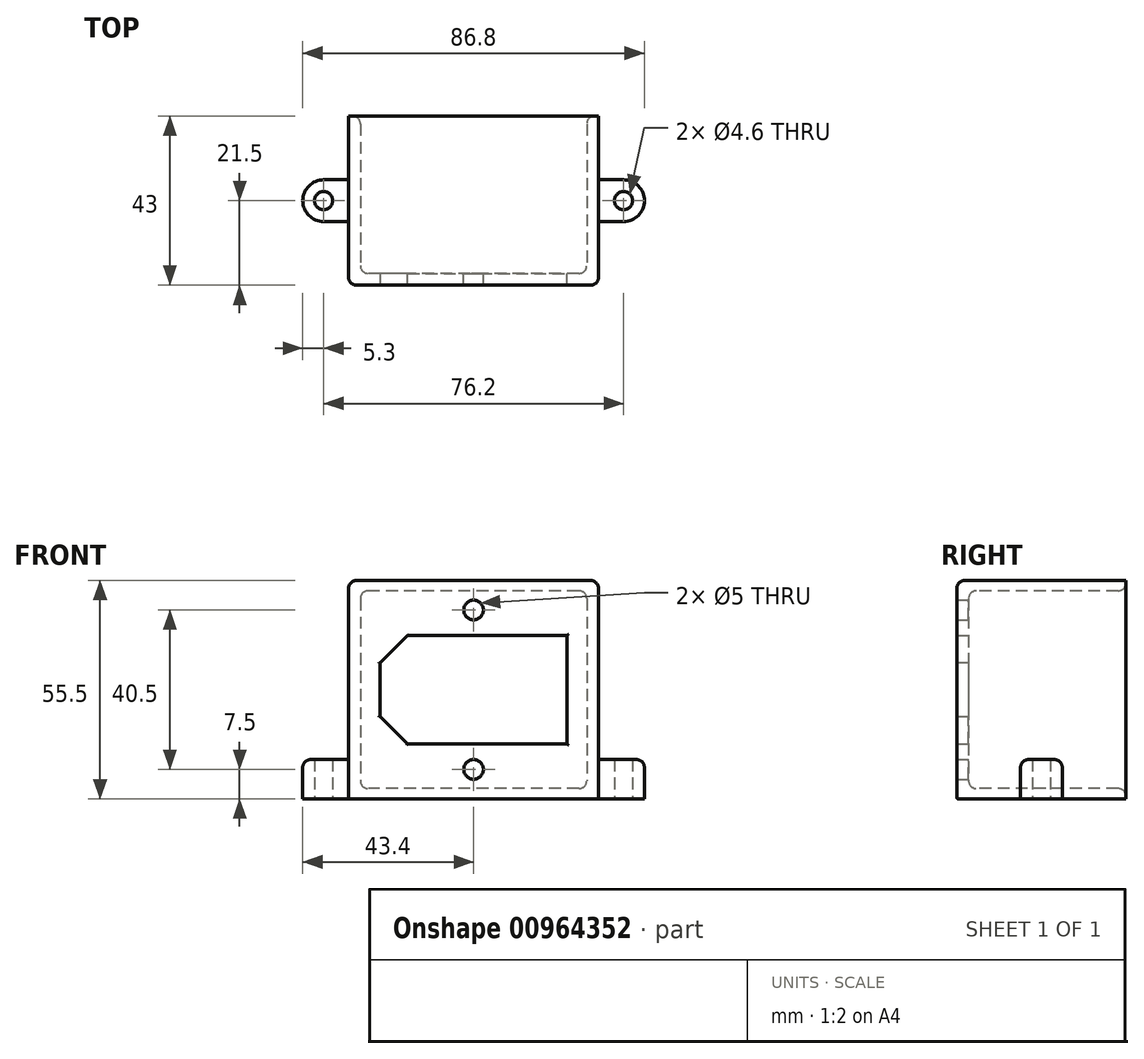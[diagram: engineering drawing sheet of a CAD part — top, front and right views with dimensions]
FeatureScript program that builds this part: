
annotation { "Feature Type Name" : "Feature", "Feature Type Description" : "" }
export const myFeature = defineFeature(function(context is Context, id is Id, definition is map)
    precondition{}
    {
        {
            var Q0;
            Q0=qCreatedBy(makeId("Front.planeOp"),FACE);
            var sketch = newSketch(context, id + "F0", { "sketchPlane" : qUnion([Q0])});
            skLineSegment(sketch, "E0.bottom", {"start": v(0, 0) * mm, "end": v(-63.5, 0) * mm});
            skLineSegment(sketch, "E0.top", {"start": v(0, 55.5) * mm, "end": v(-63.5, 55.5) * mm});
            skLineSegment(sketch, "E0.left", {"start": v(0, 0) * mm, "end": v(0, 55.5) * mm});
            skLineSegment(sketch, "E0.right", {"start": v(-63.5, 0) * mm, "end": v(-63.5, 55.5) * mm});
            skLineSegment(sketch, "E1.bottom", {"start": v(-55.5, 41.5) * mm, "end": v(-8, 41.5) * mm});
            skLineSegment(sketch, "E1.top", {"start": v(-55.5, 14) * mm, "end": v(-8, 14) * mm});
            skLineSegment(sketch, "E1.left", {"start": v(-55.5, 41.5) * mm, "end": v(-55.5, 14) * mm});
            skLineSegment(sketch, "E1.right", {"start": v(-8, 41.5) * mm, "end": v(-8, 14) * mm});
            skLineSegment(sketch, "E2", {"start": v(-31.75, 55.5) * mm, "end": v(-31.75, 0) * mm, "construction": true});
            skPoint(sketch, "E3", {"position": v(-31.75, 41.5) * mm});
            skLineSegment(sketch, "E4", {"start": v(-34.25, 55.5) * mm, "end": v(-34.25, 0) * mm, "construction": true});
            skCircle(sketch, "E5", {"center": v(-31.75, 48) * mm, "radius": 2.5 * mm});
            skCircle(sketch, "E6", {"center": v(-31.75, 7.5) * mm, "radius": 2.5 * mm});
            skLineSegment(sketch, "E7", {"start": v(-55.5, 27.75) * mm, "end": v(-8, 27.75) * mm, "construction": true});
            skLineSegment(sketch, "E8.bottom", {"start": v(-8, 48) * mm, "end": v(-55.5, 48) * mm, "construction": true});
            skLineSegment(sketch, "E8.top", {"start": v(-8, 7.5) * mm, "end": v(-55.5, 7.5) * mm, "construction": true});
            skLineSegment(sketch, "E8.left", {"start": v(-8, 48) * mm, "end": v(-8, 7.5) * mm, "construction": true});
            skLineSegment(sketch, "E8.right", {"start": v(-55.5, 48) * mm, "end": v(-55.5, 7.5) * mm, "construction": true});
            skPoint(sketch, "E8.middle", {"position": v(-31.75, 27.75) * mm});
            skLineSegment(sketch, "E9", {"start": v(0, 55.5) * mm, "end": v(-63.5, 0) * mm, "construction": true});
            skLineSegment(sketch, "E10.bottom", {"start": v(-3, 52.88) * mm, "end": v(-60.5, 52.88) * mm});
            skLineSegment(sketch, "E10.top", {"start": v(-3, 2.62) * mm, "end": v(-60.5, 2.62) * mm});
            skLineSegment(sketch, "E10.left", {"start": v(-3, 52.88) * mm, "end": v(-3, 2.62) * mm});
            skLineSegment(sketch, "E10.right", {"start": v(-60.5, 52.88) * mm, "end": v(-60.5, 2.62) * mm});
            skSolve(sketch);
        }
        {
            var Q0;
            Q0 = qSketchRegion(id + "F0", true);
            var Q1;
            Q1=makeQuery(id+"F0.imprint","IMPRINT",FACE,{"disambiguationData":[TD([[makeQuery(id+"F0.imprint","IMPRINT",EDGE,{"derivedFrom":sQuery(id+"F0.wireOp",EDGE,"E1.bottom")}),1.0]])]});
            extrude(context, id + "F1", {"entities" : qUnion([Q0, Q1]), "depth" : 3 * mm, "offsetDistance" : 25 * mm});
        }
        {
            var Q0;
            Q0=makeQuery(id+"F1.opExtrude","SWEPT_EDGE",EDGE,{"disambiguationData":[OSD([sQuery(id+"F0.wireOp",EDGE,"E1.bottom"),sQuery(id+"F0.wireOp",EDGE,"E1.left")])]});
            var Q1;
            Q1=makeQuery(id+"F1.opExtrude","SWEPT_EDGE",EDGE,{"disambiguationData":[OSD([sQuery(id+"F0.wireOp",EDGE,"E1.top"),sQuery(id+"F0.wireOp",EDGE,"E1.left")])]});
            chamfer(context, id + "F2", {"entities" : qUnion([Q0, Q1]), "width" : 7 * mm, "tangentPropagation" : true});
        }
        {
            var Q0;
            Q0=makeQuery(id+"F0.imprint","IMPRINT",FACE,{"disambiguationData":[TD([[makeQuery(id+"F0.imprint","IMPRINT",EDGE,{"derivedFrom":sQuery(id+"F0.wireOp",EDGE,"E0.bottom")}),-1.0]])]});
            extrude(context, id + "F3", {"entities" : qUnion([Q0]), "operationType" : NewBodyOperationType.ADD, "oppositeDirection" : true, "depth" : 40 * mm, "offsetDistance" : 25 * mm});
        }
        {
            var Q0;
            {var subQ0=sQuery(id+"F0.wireOp",EDGE,"E0.bottom");Q0=makeQuery(id+"F3.boolean.opBoolean","MERGE",FACE,{"derivedFrom":[makeQuery(id+"F1.opExtrude","SWEPT_FACE",FACE,{"disambiguationData":[OSD([subQ0])]}),makeQuery(id+"F3.opExtrude","SWEPT_FACE",FACE,{"disambiguationData":[OSD([subQ0])]})]});}
            var sketch = newSketch(context, id + "F4", { "sketchPlane" : qUnion([Q0])});
            skLineSegment(sketch, "E11.0.0", {"start": v(-63.5, 3) * mm, "end": v(-63.5, -40) * mm, "construction": true});
            skLineSegment(sketch, "E11.0.1", {"start": v(-63.5, -40) * mm, "end": v(0, -40) * mm, "construction": true});
            skLineSegment(sketch, "E11.0.2", {"start": v(0, -40) * mm, "end": v(0, 3) * mm, "construction": true});
            skLineSegment(sketch, "E11.0.3", {"start": v(0, 3) * mm, "end": v(-63.5, 3) * mm, "construction": true});
            skLineSegment(sketch, "E12", {"start": v(-63.5, -18.5) * mm, "end": v(0, -18.5) * mm, "construction": true});
            skLineSegment(sketch, "E13", {"start": v(0, 3) * mm, "end": v(-63.5, -40) * mm, "construction": true});
            skLineSegment(sketch, "E14.bottom", {"start": v(6.35, 7.3) * mm, "end": v(-69.85, 7.3) * mm, "construction": true});
            skLineSegment(sketch, "E14.top", {"start": v(6.35, -44.3) * mm, "end": v(-69.85, -44.3) * mm, "construction": true});
            skLineSegment(sketch, "E14.left", {"start": v(6.35, 7.3) * mm, "end": v(6.35, -44.3) * mm, "construction": true});
            skLineSegment(sketch, "E14.right", {"start": v(-69.85, 7.3) * mm, "end": v(-69.85, -44.3) * mm, "construction": true});
            skPoint(sketch, "E14.middle", {"position": v(-31.75, -18.5) * mm});
            skCircle(sketch, "E15", {"center": v(-69.85, -18.5) * mm, "radius": 2.3 * mm});
            skLineSegment(sketch, "E16", {"start": v(-63.5, -13.2) * mm, "end": v(0, -13.2) * mm, "construction": true});
            skCircle(sketch, "E17", {"center": v(-69.85, -18.5) * mm, "radius": 5.3 * mm});
            skLineSegment(sketch, "E18", {"start": v(-63.5, -16.2) * mm, "end": v(0, -16.2) * mm, "construction": true});
            skCircle(sketch, "E19", {"center": v(6.35, -18.5) * mm, "radius": 2.3 * mm});
            skCircle(sketch, "E20", {"center": v(6.35, -18.5) * mm, "radius": 5.3 * mm});
            skLineSegment(sketch, "E21", {"start": v(-69.85, -13.2) * mm, "end": v(-63.5, -13.2) * mm});
            skLineSegment(sketch, "E22", {"start": v(-69.85, -23.8) * mm, "end": v(-63.5, -23.8) * mm});
            skLineSegment(sketch, "E23", {"start": v(6.35, -13.2) * mm, "end": v(0, -13.2) * mm});
            skLineSegment(sketch, "E24", {"start": v(6.35, -23.8) * mm, "end": v(0, -23.8) * mm});
            skSolve(sketch);
        }
        {
            var Q0;
            Q0 = qSketchRegion(id + "F4", true);
            var Q1;
            {var subQ0=sQuery(id+"F4.wireOp",EDGE,"E21");Q1=makeQuery(id+"F4.imprint","IMPRINT",FACE,{"disambiguationData":[TD([[makeQuery(id+"F4.imprint","IMPRINT",EDGE,{"derivedFrom":subQ0}),-1.0]])]});}
            var Q2;
            {var subQ0=sQuery(id+"F4.wireOp",EDGE,"E23");Q2=makeQuery(id+"F4.imprint","IMPRINT",FACE,{"disambiguationData":[TD([[makeQuery(id+"F4.imprint","IMPRINT",EDGE,{"derivedFrom":subQ0}),1.0]])]});}
            var Q3;
            {var subQ0=sQuery(id+"F0.wireOp",EDGE,"E0.top");Q3=makeQuery(id+"F3.boolean.opBoolean","MERGE",FACE,{"derivedFrom":[makeQuery(id+"F1.opExtrude","SWEPT_FACE",FACE,{"disambiguationData":[OSD([subQ0])]}),makeQuery(id+"F3.opExtrude","SWEPT_FACE",FACE,{"disambiguationData":[OSD([subQ0])]})]});}
            extrude(context, id + "F5", {"entities" : qUnion([Q0, Q1, Q2]), "operationType" : NewBodyOperationType.ADD, "oppositeDirection" : true, "depth" : 10 * mm, "endBoundEntityFace" : qUnion([Q3]), "offsetDistance" : 25 * mm});
        }
        {
            var Q0;
            {var subQ0=sQuery(id+"F0.wireOp",EDGE,"E10.left");var subQ1=sQuery(id+"F0.wireOp",EDGE,"E10.top");var subQ2=sQuery(id+"F0.wireOp",EDGE,"E10.bottom");Q0=makeQuery(id+"F5.boolean.opBoolean","SPLIT",FACE,{"disambiguationData":[TD([makeQuery(id+"F3.opExtrude","CAP_FACE",FACE,{"disambiguationData":[OSD([sQuery(id+"F0.wireOp",EDGE,"E0.bottom"),sQuery(id+"F0.wireOp",EDGE,"E0.top"),sQuery(id+"F0.wireOp",EDGE,"E0.left"),sQuery(id+"F0.wireOp",EDGE,"E0.right"),subQ2,subQ1,subQ0,sQuery(id+"F0.wireOp",EDGE,"E10.right")])],"isStart":false})])],"derivedFrom":makeQuery(id+"F3.opExtrude","SWEPT_FACE",FACE,{"disambiguationData":[OSD([subQ0])]})});}
            var Q1;
            Q1=makeQuery(id+"F5.boolean.opBoolean","SPLIT",FACE,{"disambiguationData":[TD([makeQuery(id+"F1.opExtrude","CAP_FACE",FACE,{"disambiguationData":[OSD([sQuery(id+"F0.wireOp",EDGE,"E0.bottom"),sQuery(id+"F0.wireOp",EDGE,"E0.top"),sQuery(id+"F0.wireOp",EDGE,"E0.left"),sQuery(id+"F0.wireOp",EDGE,"E0.right"),sQuery(id+"F0.wireOp",EDGE,"E1.bottom"),sQuery(id+"F0.wireOp",EDGE,"E1.top"),sQuery(id+"F0.wireOp",EDGE,"E1.left"),sQuery(id+"F0.wireOp",EDGE,"E1.right"),sQuery(id+"F0.wireOp",EDGE,"E5"),sQuery(id+"F0.wireOp",EDGE,"E6")])],"isStart":true})])],"derivedFrom":makeQuery(id+"F3.opExtrude","SWEPT_FACE",FACE,{"disambiguationData":[OSD([sQuery(id+"F0.wireOp",EDGE,"E10.left")])]})});
            var Q2;
            {var subQ2=sQuery(id+"F0.wireOp",EDGE,"E10.top");Q2=makeQuery(id+"F5.boolean.opBoolean","SPLIT",FACE,{"disambiguationData":[TD([makeQuery(id+"F5.opExtrude","SWEPT_FACE",FACE,{"disambiguationData":[OSD([sQuery(id+"F4.wireOp",EDGE,"E17")])]})])],"derivedFrom":makeQuery(id+"F3.opExtrude","SWEPT_FACE",FACE,{"disambiguationData":[OSD([subQ2])]})});}
            var Q3;
            {var subQ2=sQuery(id+"F0.wireOp",EDGE,"E10.bottom");Q3=makeQuery(id+"F5.boolean.opBoolean","SPLIT",FACE,{"disambiguationData":[TD([makeQuery(id+"F5.opExtrude","SWEPT_FACE",FACE,{"disambiguationData":[OSD([sQuery(id+"F4.wireOp",EDGE,"E17")])]})])],"derivedFrom":makeQuery(id+"F3.opExtrude","SWEPT_FACE",FACE,{"disambiguationData":[OSD([subQ2])]})});}
            var Q4;
            {var subQ0=sQuery(id+"F0.wireOp",EDGE,"E10.right");var subQ1=sQuery(id+"F0.wireOp",EDGE,"E10.top");var subQ2=sQuery(id+"F0.wireOp",EDGE,"E10.bottom");Q4=makeQuery(id+"F5.boolean.opBoolean","SPLIT",FACE,{"disambiguationData":[TD([makeQuery(id+"F3.opExtrude","CAP_FACE",FACE,{"disambiguationData":[OSD([sQuery(id+"F0.wireOp",EDGE,"E0.bottom"),sQuery(id+"F0.wireOp",EDGE,"E0.top"),sQuery(id+"F0.wireOp",EDGE,"E0.left"),sQuery(id+"F0.wireOp",EDGE,"E0.right"),subQ2,subQ1,sQuery(id+"F0.wireOp",EDGE,"E10.left"),subQ0])],"isStart":false})])],"derivedFrom":makeQuery(id+"F3.opExtrude","SWEPT_FACE",FACE,{"disambiguationData":[OSD([subQ0])]})});}
            var Q5;
            Q5=makeQuery(id+"F5.boolean.opBoolean","SPLIT",FACE,{"disambiguationData":[TD([makeQuery(id+"F1.opExtrude","CAP_FACE",FACE,{"disambiguationData":[OSD([sQuery(id+"F0.wireOp",EDGE,"E0.bottom"),sQuery(id+"F0.wireOp",EDGE,"E0.top"),sQuery(id+"F0.wireOp",EDGE,"E0.left"),sQuery(id+"F0.wireOp",EDGE,"E0.right"),sQuery(id+"F0.wireOp",EDGE,"E1.bottom"),sQuery(id+"F0.wireOp",EDGE,"E1.top"),sQuery(id+"F0.wireOp",EDGE,"E1.left"),sQuery(id+"F0.wireOp",EDGE,"E1.right"),sQuery(id+"F0.wireOp",EDGE,"E5"),sQuery(id+"F0.wireOp",EDGE,"E6")])],"isStart":true})])],"derivedFrom":makeQuery(id+"F3.opExtrude","SWEPT_FACE",FACE,{"disambiguationData":[OSD([sQuery(id+"F0.wireOp",EDGE,"E10.right")])]})});
            var Q6;
            {var subQ0=sQuery(id+"F0.wireOp",EDGE,"E0.right");var subQ1=sQuery(id+"F0.wireOp",EDGE,"E0.top");Q6=makeQuery(id+"F5.boolean.opBoolean","SPLIT",EDGE,{"disambiguationData":[TD([makeQuery(id+"F3.opExtrude","CAP_FACE",FACE,{"disambiguationData":[OSD([sQuery(id+"F0.wireOp",EDGE,"E0.bottom"),subQ1,sQuery(id+"F0.wireOp",EDGE,"E0.left"),subQ0,sQuery(id+"F0.wireOp",EDGE,"E10.bottom"),sQuery(id+"F0.wireOp",EDGE,"E10.top"),sQuery(id+"F0.wireOp",EDGE,"E10.left"),sQuery(id+"F0.wireOp",EDGE,"E10.right")])],"isStart":false})])],"derivedFrom":makeQuery(id+"F3.boolean.opBoolean","MERGE",EDGE,{"derivedFrom":[makeQuery(id+"F1.opExtrude","SWEPT_EDGE",EDGE,{"disambiguationData":[OSD([subQ1,subQ0])]}),makeQuery(id+"F3.opExtrude","SWEPT_EDGE",EDGE,{"disambiguationData":[OSD([subQ1,subQ0])]})]})});}
            var Q7;
            {var subQ0=sQuery(id+"F0.wireOp",EDGE,"E0.top");var subQ1=sQuery(id+"F0.wireOp",EDGE,"E0.right");Q7=makeQuery(id+"F5.boolean.opBoolean","SPLIT",EDGE,{"disambiguationData":[TD([makeQuery(id+"F1.opExtrude","CAP_FACE",FACE,{"disambiguationData":[OSD([sQuery(id+"F0.wireOp",EDGE,"E0.bottom"),subQ0,sQuery(id+"F0.wireOp",EDGE,"E0.left"),subQ1,sQuery(id+"F0.wireOp",EDGE,"E1.bottom"),sQuery(id+"F0.wireOp",EDGE,"E1.top"),sQuery(id+"F0.wireOp",EDGE,"E1.left"),sQuery(id+"F0.wireOp",EDGE,"E1.right"),sQuery(id+"F0.wireOp",EDGE,"E5"),sQuery(id+"F0.wireOp",EDGE,"E6")])],"isStart":false})])],"derivedFrom":makeQuery(id+"F3.boolean.opBoolean","MERGE",EDGE,{"derivedFrom":[makeQuery(id+"F1.opExtrude","SWEPT_EDGE",EDGE,{"disambiguationData":[OSD([subQ0,subQ1])]}),makeQuery(id+"F3.opExtrude","SWEPT_EDGE",EDGE,{"disambiguationData":[OSD([subQ0,subQ1])]})]})});}
            var Q8;
            Q8=makeQuery(id+"F5.opExtrude","CAP_EDGE",EDGE,{"disambiguationData":[OSD([sQuery(id+"F4.wireOp",EDGE,"E17")])],"isStart":false});
            var Q9;
            {var subQ0=sQuery(id+"F0.wireOp",EDGE,"E0.top");Q9=makeQuery(id+"F5.boolean.opBoolean","MERGE",FACE,{"derivedFrom":[makeQuery(id+"F3.boolean.opBoolean","MERGE",FACE,{"derivedFrom":[makeQuery(id+"F1.opExtrude","SWEPT_FACE",FACE,{"disambiguationData":[OSD([subQ0])]}),makeQuery(id+"F3.opExtrude","SWEPT_FACE",FACE,{"disambiguationData":[OSD([subQ0])]})]}),makeQuery(id+"F5.opExtrude","CAP_FACE",FACE,{"disambiguationData":[OSD([sQuery(id+"F4.wireOp",EDGE,"E15"),sQuery(id+"F4.wireOp",EDGE,"E17")])],"isStart":false}),makeQuery(id+"F5.opExtrude","CAP_FACE",FACE,{"disambiguationData":[OSD([sQuery(id+"F4.wireOp",EDGE,"E19"),sQuery(id+"F4.wireOp",EDGE,"E20")])],"isStart":false})]});}
            var Q10;
            {var subQ0=sQuery(id+"F0.wireOp",EDGE,"E0.left");Q10=makeQuery(id+"F5.boolean.opBoolean","INTERSECT",EDGE,{"disambiguationData":[OD(0.0)],"derivedFrom":[makeQuery(id+"F3.boolean.opBoolean","MERGE",FACE,{"derivedFrom":[makeQuery(id+"F1.opExtrude","SWEPT_FACE",FACE,{"disambiguationData":[OSD([subQ0])]}),makeQuery(id+"F3.opExtrude","SWEPT_FACE",FACE,{"disambiguationData":[OSD([subQ0])]})]}),makeQuery(id+"F5.opExtrude","SWEPT_FACE",FACE,{"disambiguationData":[OSD([sQuery(id+"F4.wireOp",EDGE,"E20")])]})]});}
            var Q11;
            {var subQ0=sQuery(id+"F0.wireOp",EDGE,"E0.left");Q11=makeQuery(id+"F5.boolean.opBoolean","INTERSECT",EDGE,{"disambiguationData":[OD(1.0)],"derivedFrom":[makeQuery(id+"F3.boolean.opBoolean","MERGE",FACE,{"derivedFrom":[makeQuery(id+"F1.opExtrude","SWEPT_FACE",FACE,{"disambiguationData":[OSD([subQ0])]}),makeQuery(id+"F3.opExtrude","SWEPT_FACE",FACE,{"disambiguationData":[OSD([subQ0])]})]}),makeQuery(id+"F5.opExtrude","SWEPT_FACE",FACE,{"disambiguationData":[OSD([sQuery(id+"F4.wireOp",EDGE,"E20")])]})]});}
            var Q12;
            {var subQ0=sQuery(id+"F0.wireOp",EDGE,"E0.right");Q12=makeQuery(id+"F5.boolean.opBoolean","INTERSECT",EDGE,{"disambiguationData":[OD(0.0)],"derivedFrom":[makeQuery(id+"F3.boolean.opBoolean","MERGE",FACE,{"derivedFrom":[makeQuery(id+"F1.opExtrude","SWEPT_FACE",FACE,{"disambiguationData":[OSD([subQ0])]}),makeQuery(id+"F3.opExtrude","SWEPT_FACE",FACE,{"disambiguationData":[OSD([subQ0])]})]}),makeQuery(id+"F5.opExtrude","SWEPT_FACE",FACE,{"disambiguationData":[OSD([sQuery(id+"F4.wireOp",EDGE,"E17")])]})]});}
            var Q13;
            {var subQ0=sQuery(id+"F0.wireOp",EDGE,"E0.right");Q13=makeQuery(id+"F5.boolean.opBoolean","INTERSECT",EDGE,{"disambiguationData":[OD(1.0)],"derivedFrom":[makeQuery(id+"F3.boolean.opBoolean","MERGE",FACE,{"derivedFrom":[makeQuery(id+"F1.opExtrude","SWEPT_FACE",FACE,{"disambiguationData":[OSD([subQ0])]}),makeQuery(id+"F3.opExtrude","SWEPT_FACE",FACE,{"disambiguationData":[OSD([subQ0])]})]}),makeQuery(id+"F5.opExtrude","SWEPT_FACE",FACE,{"disambiguationData":[OSD([sQuery(id+"F4.wireOp",EDGE,"E17")])]})]});}
            var Q14;
            Q14=makeQuery(id+"F5.opExtrude","CAP_EDGE",EDGE,{"disambiguationData":[OSD([sQuery(id+"F4.wireOp",EDGE,"E20")])],"isStart":false});
            var Q15;
            {var subQ0=sQuery(id+"F0.wireOp",EDGE,"E0.left");var subQ1=sQuery(id+"F0.wireOp",EDGE,"E0.top");Q15=makeQuery(id+"F3.boolean.opBoolean","MERGE",EDGE,{"derivedFrom":[makeQuery(id+"F1.opExtrude","SWEPT_EDGE",EDGE,{"disambiguationData":[OSD([subQ1,subQ0])]}),makeQuery(id+"F3.opExtrude","SWEPT_EDGE",EDGE,{"disambiguationData":[OSD([subQ1,subQ0])]})]});}
            var Q16;
            Q16=makeQuery(id+"F1.opExtrude","CAP_EDGE",EDGE,{"disambiguationData":[OSD([sQuery(id+"F0.wireOp",EDGE,"E0.left")])],"isStart":false});
            var Q17;
            Q17=makeQuery(id+"F1.opExtrude","CAP_EDGE",EDGE,{"disambiguationData":[OSD([sQuery(id+"F0.wireOp",EDGE,"E0.right")])],"isStart":false});
            var Q18;
            Q18=makeQuery(id+"F1.opExtrude","CAP_EDGE",EDGE,{"disambiguationData":[OSD([sQuery(id+"F0.wireOp",EDGE,"E0.top")])],"isStart":false});
            var Q19;
            Q19=makeQuery(id+"F5.opExtrude","SWEPT_EDGE",EDGE,{"disambiguationData":[OSD([sQuery(id+"F0.wireOp",EDGE,"E0.bottom"),sQuery(id+"F0.wireOp",EDGE,"E0.right"),sQuery(id+"F4.wireOp",EDGE,"E21")])]});
            var Q20;
            Q20=makeQuery(id+"F5.opExtrude","SWEPT_EDGE",EDGE,{"disambiguationData":[OSD([sQuery(id+"F0.wireOp",EDGE,"E0.bottom"),sQuery(id+"F0.wireOp",EDGE,"E0.left"),sQuery(id+"F4.wireOp",EDGE,"E23")])]});
            fillet(context, id + "F6", {"entities" : qUnion([Q0, Q1, Q2, Q3, Q4, Q5, Q6, Q7, Q8, Q9, Q10, Q11, Q12, Q13, Q14, Q15, Q16, Q17, Q18, Q19, Q20]), "tangentPropagation" : true, "radius" : 2 * mm, "defaultsChanged" : false, "vertexSettings" : [], "allowEdgeOverflow" : false});
        }
        {
            var Q0;
            Q0=makeQuery(id+"F1.opExtrude","CAP_FACE",FACE,{"disambiguationData":[OSD([sQuery(id+"F0.wireOp",EDGE,"E0.bottom"),sQuery(id+"F0.wireOp",EDGE,"E0.top"),sQuery(id+"F0.wireOp",EDGE,"E0.left"),sQuery(id+"F0.wireOp",EDGE,"E0.right"),sQuery(id+"F0.wireOp",EDGE,"E1.bottom"),sQuery(id+"F0.wireOp",EDGE,"E1.top"),sQuery(id+"F0.wireOp",EDGE,"E1.left"),sQuery(id+"F0.wireOp",EDGE,"E1.right"),sQuery(id+"F0.wireOp",EDGE,"E5"),sQuery(id+"F0.wireOp",EDGE,"E6")])],"isStart":false});
            var Q1;
            Q1=makeQuery(id+"FSLBBleyA1LKpYb_1.boolean.opBoolean","COPY",EDGE,{"derivedFrom":makeQuery(id+"FSLBBleyA1LKpYb_1.opExtrude","CAP_EDGE",EDGE,{"disambiguationData":[OSD([sQuery(id+"F4.wireOp",EDGE,"E15")])],"isStart":true})});
            var Q2;
            Q2=makeQuery(id+"FSLBBleyA1LKpYb_1.boolean.opBoolean","COPY",EDGE,{"derivedFrom":makeQuery(id+"FSLBBleyA1LKpYb_1.opExtrude","CAP_EDGE",EDGE,{"disambiguationData":[OSD([sQuery(id+"F4.wireOp",EDGE,"E19")])],"isStart":true})});
            fillet(context, id + "F7", {"entities" : qUnion([Q0, Q1, Q2]), "tangentPropagation" : true, "radius" : .3 * mm, "defaultsChanged" : false, "vertexSettings" : [], "allowEdgeOverflow" : false});
        }
    });
